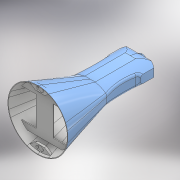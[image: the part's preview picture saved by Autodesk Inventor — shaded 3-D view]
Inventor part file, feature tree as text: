
AUTODESK INVENTOR PART (.ipt)
format: ipt  version: 2017 (Build 210142000, 142)  size: 1,122,304 bytes
history: native  units: mm
features: sketch x13, extrude x11, projected_geometry x5, plane x3, fillet x1, loft x1, mirror x1, shell x1, other x1
ambient origin geometry x8: Origin, YZ Plane, XZ Plane, XY Plane, X Axis, Y Axis, Z Axis, Center Point
bodies: Solid1 (feature_tree)
feature tree (37):
  extrude  "Extrusion1"  Depth=35.0mm
  extrude  "Extrusion2"  Depth=9.0mm TaperAngle=0.0deg
  extrude  "Extrusion6"  Depth=70.0mm TaperAngle=0.0deg
  extrude  "Extrusion9"  Depth=10.0mm
  extrude  "Extrusion11"  Depth=200.0mm
  fillet  "Fillet2"  [1 undecoded]
  sketch  "Sketch29"  dims[d72=0.0mm d73=90.0deg d81=2.0mm d83=-324.476mm]
  plane  "Work Plane8"
  loft  "Loft1"
  mirror  "Mirror8"
  shell  "Shell3"  Thickness=-324.476mm
  plane  "Work Plane9"
  extrude  "Extrusion16"  [1 undecoded]
  plane  "Work Plane10"
  extrude  "Extrusion17"  Depth=1.5mm TaperAngle=0.0deg
  extrude  "Extrusion18"  Depth=3.0mm TaperAngle=0.0deg
  extrude  "Extrusion19"  [1 undecoded]
  extrude  "Extrusion20"  [1 undecoded]
  extrude  "Extrusion21"  [1 undecoded]
  sketch  "Sketch1"  dims[d0=63.0mm d1=0.0mm d2=35.0mm]
  sketch  "Sketch3"  dims[d3=150.0mm d4=9.0mm d5=0.0mm]
  sketch  "Sketch12"  dims[d30=250.0mm d31=0.0mm d48=70.0mm d49=0.0mm]
  sketch  "Sketch17"  dims[d53=70.0mm d54=0.0mm d55=10.0mm]
  sketch  "Sketch20"  dims[d68=-347.0mm d69=200.0mm d70=0.0mm d71=90.0deg]
  projected_geometry  "Projected Loop9"
  sketch  "Sketch30"  dims[d93=2.5mm d94=0.0mm d96=-15.524mm]
  other  "Edges1"
  sketch  "Sketch37"  dims[d102=4.0mm d103=0.0mm d104=1.5mm d105=0.0mm]
  sketch  "Sketch38"  dims[d106=2.0mm d107=0.0mm d111=3.0mm d112=0.0mm]
  sketch  "Sketch39"  dims[d113=12.0mm d114=0.0mm]
  projected_geometry  "Projected Loop13"
  projected_geometry  "Projected Loop14"
  sketch  "Sketch41"
  sketch  "Sketch43"
  sketch  "Sketch44"
  projected_geometry  "Projected Loop15"
  projected_geometry  "Projected Loop16"
note: 5 required parameter values undecoded (feature->parameter linkage not recoverable at this tier; creation-order binding heuristic only, values carry confidence <= 0.55)
